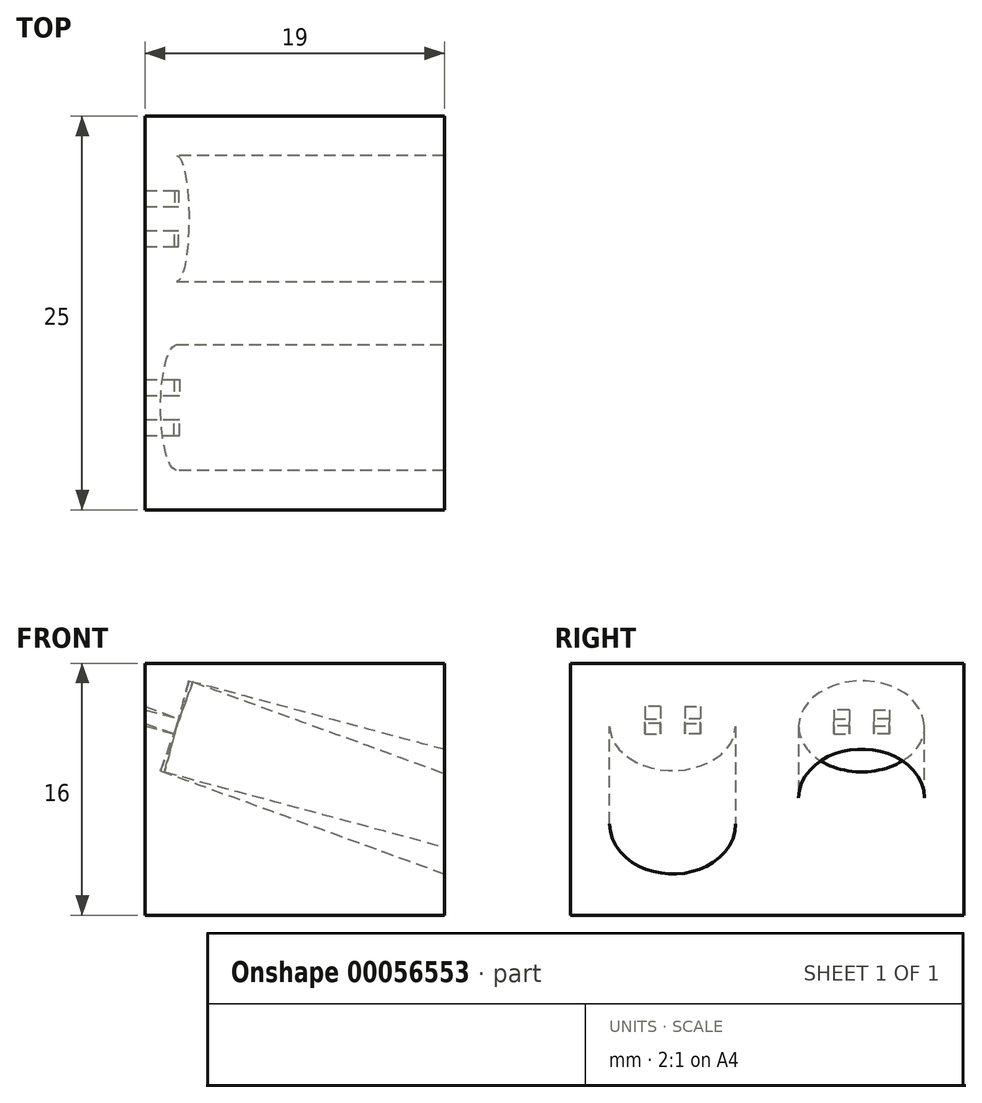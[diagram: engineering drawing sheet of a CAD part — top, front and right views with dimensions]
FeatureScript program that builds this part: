
annotation { "Feature Type Name" : "Feature", "Feature Type Description" : "" }
export const myFeature = defineFeature(function(context is Context, id is Id, definition is map)
    precondition{}
    {
        {
            var Q0;
            Q0=qCreatedBy(makeId("Top.planeOp"),FACE);
            var sketch = newSketch(context, id + "F0", { "sketchPlane" : qUnion([Q0])});
            skLineSegment(sketch, "E0.bottom", {"start": v(0, 0) * mm, "end": v(19, 0) * mm});
            skLineSegment(sketch, "E0.top", {"start": v(0, 25) * mm, "end": v(19, 25) * mm});
            skLineSegment(sketch, "E0.left", {"start": v(0, 0) * mm, "end": v(0, 25) * mm});
            skLineSegment(sketch, "E0.right", {"start": v(19, 0) * mm, "end": v(19, 25) * mm});
            skSolve(sketch);
        }
        {
            var Q0;
            Q0=makeQuery(id+"F0.imprint","IMPRINT",FACE,{"disambiguationData":[TD([[makeQuery(id+"F0.imprint","IMPRINT",EDGE,{"derivedFrom":sQuery(id+"F0.wireOp",EDGE,"E0.bottom")}),1.0]])]});
            extrude(context, id + "F1", {"entities" : qUnion([Q0]), "depth" : 16 * mm});
        }
        {
            var Q0;
            Q0=qCreatedBy(makeId("Right.planeOp"),FACE);
            cPlane(context, id + "F2", {"entities" : qUnion([Q0]), "cplaneType" : CPlaneType.OFFSET, "offset" : 2 * mm, "width" : 150 * mm, "height" : 150 * mm});
        }
        {
            var Q0;
            Q0=qCreatedBy(id+"F2.planeOp",FACE);
            var sketch = newSketch(context, id + "F3", { "sketchPlane" : qUnion([Q0])});
            skPoint(sketch, "E1", {"position": v(12.5, 0) * mm});
            skPoint(sketch, "E2", {"position": v(12.5, 12) * mm});
            skPoint(sketch, "E3", {"position": v(18.5, 12) * mm});
            skPoint(sketch, "E4", {"position": v(6.5, 12) * mm});
            skLineSegment(sketch, "E5", {"start": v(18.5, 12) * mm, "end": v(19.75, 12) * mm});
            skLineSegment(sketch, "E6", {"start": v(6.5, 12) * mm, "end": v(3.86, 12) * mm});
            skSolve(sketch);
        }
        {
            var Q0;
            Q0=sQuery(id+"F3.wireOp",EDGE,"E5");
            cPlane(context, id + "F4", {"entities" : qUnion([Q0]), "cplaneType" : CPlaneType.LINE_ANGLE, "offset" : 150 * mm, "angle" : 105 * degree, "width" : 150 * mm, "height" : 150 * mm});
        }
        {
            var Q0;
            Q0=sQuery(id+"F3.wireOp",EDGE,"E6");
            cPlane(context, id + "F5", {"entities" : qUnion([Q0]), "cplaneType" : CPlaneType.LINE_ANGLE, "offset" : 150 * mm, "angle" : 70 * degree, "width" : 150 * mm, "height" : 150 * mm});
        }
        {
            var Q0;
            Q0=qCreatedBy(id+"F4.planeOp",FACE);
            var sketch = newSketch(context, id + "F6", { "sketchPlane" : qUnion([Q0])});
            skPoint(sketch, "E7", {"position": v(18.5, 12.1) * mm});
            skPoint(sketch, "E8", {"position": v(22.5, 12.1) * mm});
            skPoint(sketch, "E9", {"position": v(18.5, 15.1) * mm});
            skEllipse(sketch, "E10", {"center": v(18.5, 12.1) * mm, "majorRadius": 4 * mm, "minorRadius": 3 * mm, "majorAxis": v(1, 0)});
            skSolve(sketch);
        }
        {
            var Q0;
            Q0=qCreatedBy(id+"F5.planeOp",FACE);
            var sketch = newSketch(context, id + "F7", { "sketchPlane" : qUnion([Q0])});
            skPoint(sketch, "E11", {"position": v(6.5, 11.96) * mm});
            skPoint(sketch, "E12", {"position": v(2.5, 11.96) * mm});
            skPoint(sketch, "E13", {"position": v(6.5, 14.96) * mm});
            skEllipse(sketch, "E14", {"center": v(6.5, 11.96) * mm, "majorRadius": 4 * mm, "minorRadius": 3 * mm, "majorAxis": v(-1, 0)});
            skSolve(sketch);
        }
        {
            var Q0;
            Q0 = qSketchRegion(id + "F6", true);
            extrude(context, id + "F8", {"entities" : qUnion([Q0]), "operationType" : NewBodyOperationType.REMOVE, "endBound" : BoundingType.THROUGH_ALL, "depth" : 25 * mm});
        }
        {
            var Q0;
            Q0 = qSketchRegion(id + "F7", true);
            extrude(context, id + "F9", {"entities" : qUnion([Q0]), "operationType" : NewBodyOperationType.REMOVE, "endBound" : BoundingType.THROUGH_ALL, "depth" : 25 * mm});
        }
        {
            var Q0;
            Q0=qCreatedBy(id+"F5.planeOp",FACE);
            var sketch = newSketch(context, id + "F10", { "sketchPlane" : qUnion([Q0])});
            skPoint(sketch, "E15", {"position": v(6.5, 11.96) * mm});
            skPoint(sketch, "E16", {"position": v(7.77, 11.96) * mm});
            skPoint(sketch, "E17", {"position": v(5.23, 11.96) * mm});
            skLineSegment(sketch, "E18.rect.bottom", {"start": v(8.27, 11.46) * mm, "end": v(7.27, 11.46) * mm});
            skLineSegment(sketch, "E18.rect.top", {"start": v(8.27, 12.46) * mm, "end": v(7.27, 12.46) * mm});
            skLineSegment(sketch, "E18.rect.left", {"start": v(8.27, 11.46) * mm, "end": v(8.27, 12.46) * mm});
            skLineSegment(sketch, "E18.rect.right", {"start": v(7.27, 11.46) * mm, "end": v(7.27, 12.46) * mm});
            skLineSegment(sketch, "E19.rect.bottom", {"start": v(4.73, 11.46) * mm, "end": v(5.73, 11.46) * mm});
            skLineSegment(sketch, "E19.rect.top", {"start": v(4.73, 12.46) * mm, "end": v(5.73, 12.46) * mm});
            skLineSegment(sketch, "E19.rect.left", {"start": v(4.73, 11.46) * mm, "end": v(4.73, 12.46) * mm});
            skLineSegment(sketch, "E19.rect.right", {"start": v(5.73, 11.46) * mm, "end": v(5.73, 12.46) * mm});
            skSolve(sketch);
        }
        {
            var Q0;
            Q0=qCreatedBy(id+"F4.planeOp",FACE);
            var sketch = newSketch(context, id + "F11", { "sketchPlane" : qUnion([Q0])});
            skPoint(sketch, "E20", {"position": v(18.5, 12.1) * mm});
            skPoint(sketch, "E21", {"position": v(19.77, 12.1) * mm});
            skPoint(sketch, "E22", {"position": v(17.23, 12.1) * mm});
            skLineSegment(sketch, "E23.rect.bottom", {"start": v(16.73, 11.6) * mm, "end": v(17.73, 11.6) * mm});
            skLineSegment(sketch, "E23.rect.top", {"start": v(16.73, 12.6) * mm, "end": v(17.73, 12.6) * mm});
            skLineSegment(sketch, "E23.rect.left", {"start": v(16.73, 11.6) * mm, "end": v(16.73, 12.6) * mm});
            skLineSegment(sketch, "E23.rect.right", {"start": v(17.73, 11.6) * mm, "end": v(17.73, 12.6) * mm});
            skLineSegment(sketch, "E24.rect.bottom", {"start": v(20.27, 11.6) * mm, "end": v(19.27, 11.6) * mm});
            skLineSegment(sketch, "E24.rect.top", {"start": v(20.27, 12.6) * mm, "end": v(19.27, 12.6) * mm});
            skLineSegment(sketch, "E24.rect.left", {"start": v(20.27, 11.6) * mm, "end": v(20.27, 12.6) * mm});
            skLineSegment(sketch, "E24.rect.right", {"start": v(19.27, 11.6) * mm, "end": v(19.27, 12.6) * mm});
            skSolve(sketch);
        }
        {
            var Q0;
            Q0 = qSketchRegion(id + "F10", true);
            extrude(context, id + "F12", {"entities" : qUnion([Q0]), "operationType" : NewBodyOperationType.REMOVE, "endBound" : BoundingType.THROUGH_ALL, "oppositeDirection" : true, "depth" : 25 * mm});
        }
        {
            var Q0;
            Q0 = qSketchRegion(id + "F11", true);
            extrude(context, id + "F13", {"entities" : qUnion([Q0]), "operationType" : NewBodyOperationType.REMOVE, "endBound" : BoundingType.THROUGH_ALL, "oppositeDirection" : true, "depth" : 25 * mm});
        }
    });
